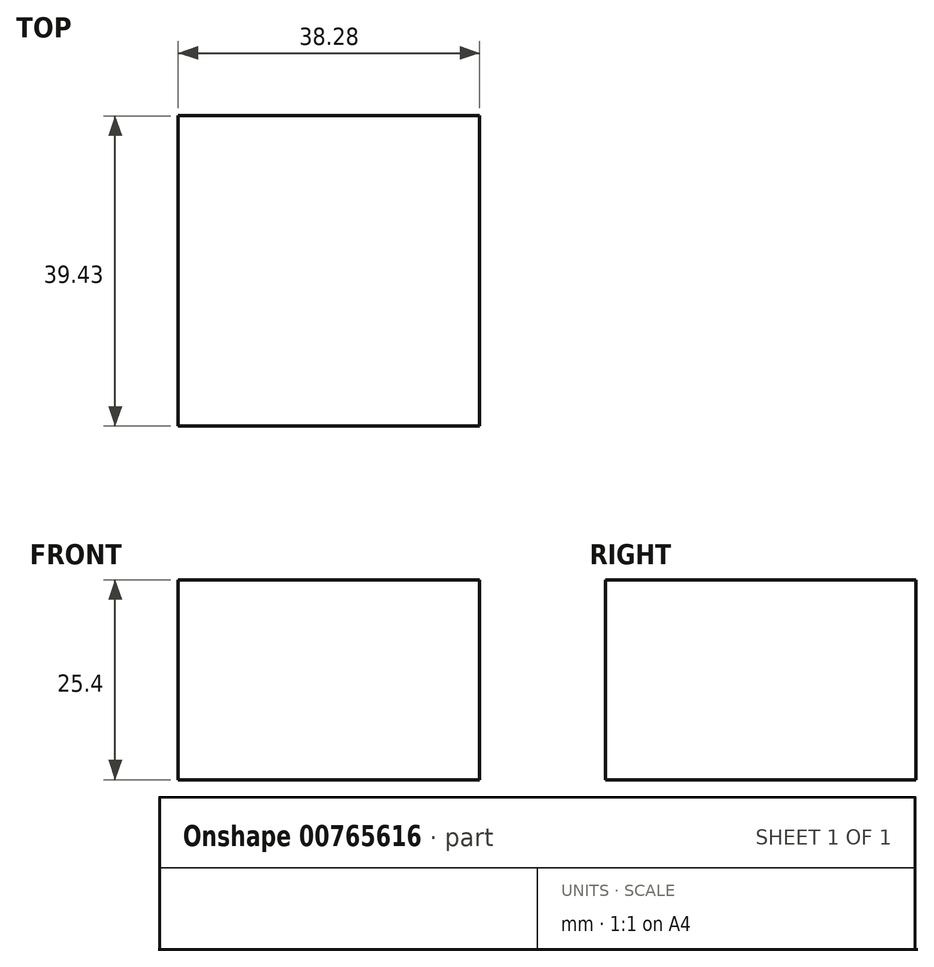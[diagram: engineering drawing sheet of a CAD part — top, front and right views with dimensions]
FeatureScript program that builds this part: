
annotation { "Feature Type Name" : "Feature", "Feature Type Description" : "" }
export const myFeature = defineFeature(function(context is Context, id is Id, definition is map)
    precondition{}
    {
        {
            var Q0;
            Q0=qCreatedBy(makeId("Top.planeOp"),FACE);
            var sketch = newSketch(context, id + "F0", { "sketchPlane" : qUnion([Q0])});
            skLineSegment(sketch, "E0.bottom", {"start": v(0, 0) * mm, "end": v(38.28, 0) * mm});
            skLineSegment(sketch, "E0.top", {"start": v(0, 39.43) * mm, "end": v(38.28, 39.43) * mm});
            skLineSegment(sketch, "E0.left", {"start": v(0, 0) * mm, "end": v(0, 39.43) * mm});
            skLineSegment(sketch, "E0.right", {"start": v(38.28, 0) * mm, "end": v(38.28, 39.43) * mm});
            skSolve(sketch);
        }
        {
            var Q0;
            Q0 = qSketchRegion(id + "F0", true);
            extrude(context, id + "F1", {"entities" : qUnion([Q0]), "depth" : 25.4 * mm, "offsetDistance" : 25.4 * mm});
        }
    });
